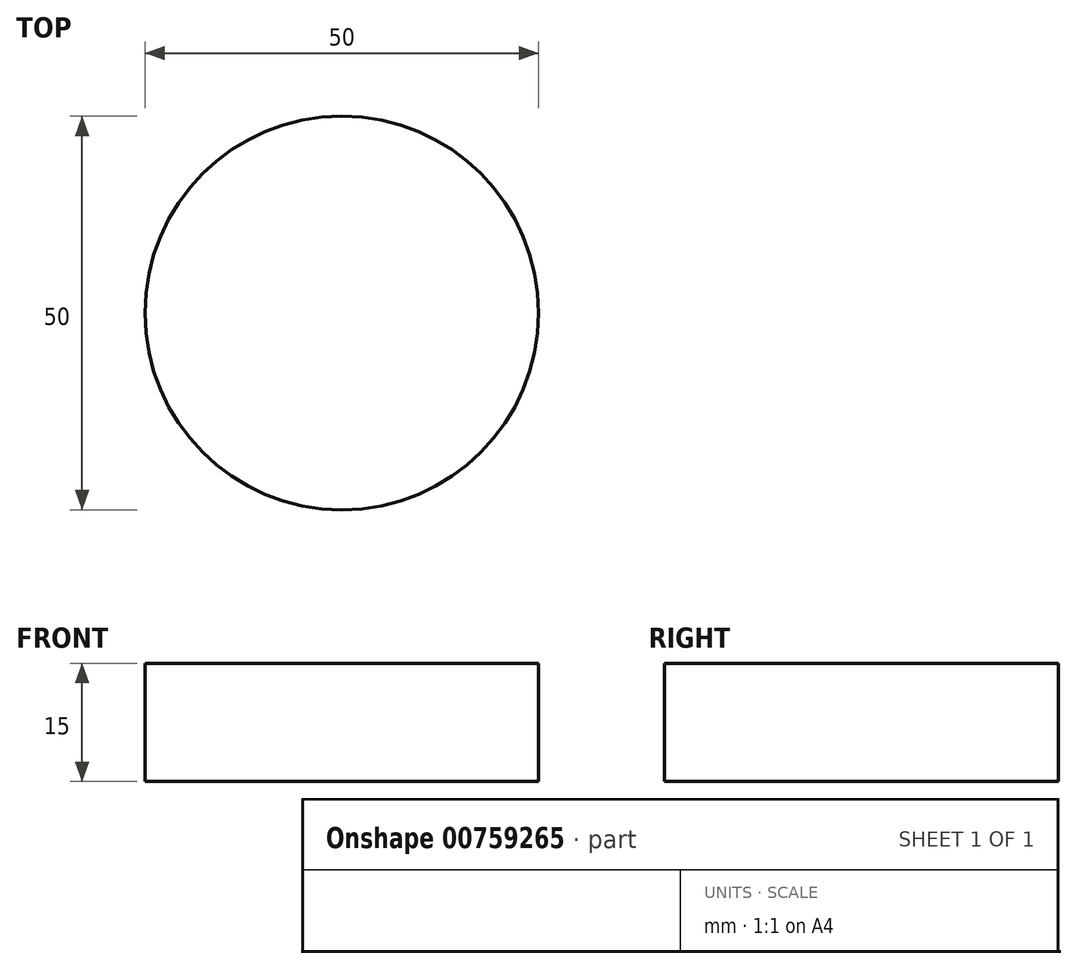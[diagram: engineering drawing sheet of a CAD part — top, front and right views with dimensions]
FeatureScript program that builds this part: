
annotation { "Feature Type Name" : "Feature", "Feature Type Description" : "" }
export const myFeature = defineFeature(function(context is Context, id is Id, definition is map)
    precondition{}
    {
        {
            var Q0;
            Q0=qCreatedBy(makeId("Top.planeOp"),FACE);
            var sketch = newSketch(context, id + "F0", { "sketchPlane" : qUnion([Q0])});
            skCircle(sketch, "E0", {"center": v(0, 0) * mm, "radius": 25 * mm});
            skSolve(sketch);
        }
        {
            var Q0;
            Q0=makeQuery(id+"F0.imprint","IMPRINT",FACE,{"disambiguationData":[TD([[makeQuery(id+"F0.imprint","IMPRINT",EDGE,{"derivedFrom":sQuery(id+"F0.wireOp",EDGE,"E0")}),1.0]])]});
            var Q1;
            Q1=sQuery(id+"F0.wireOp",EDGE,"E0");
            extrude(context, id + "F1", {"entities" : qUnion([Q0]), "surfaceEntities" : qUnion([Q1]), "depth" : 15 * mm, "offsetDistance" : 25.4 * mm});
        }
    });
